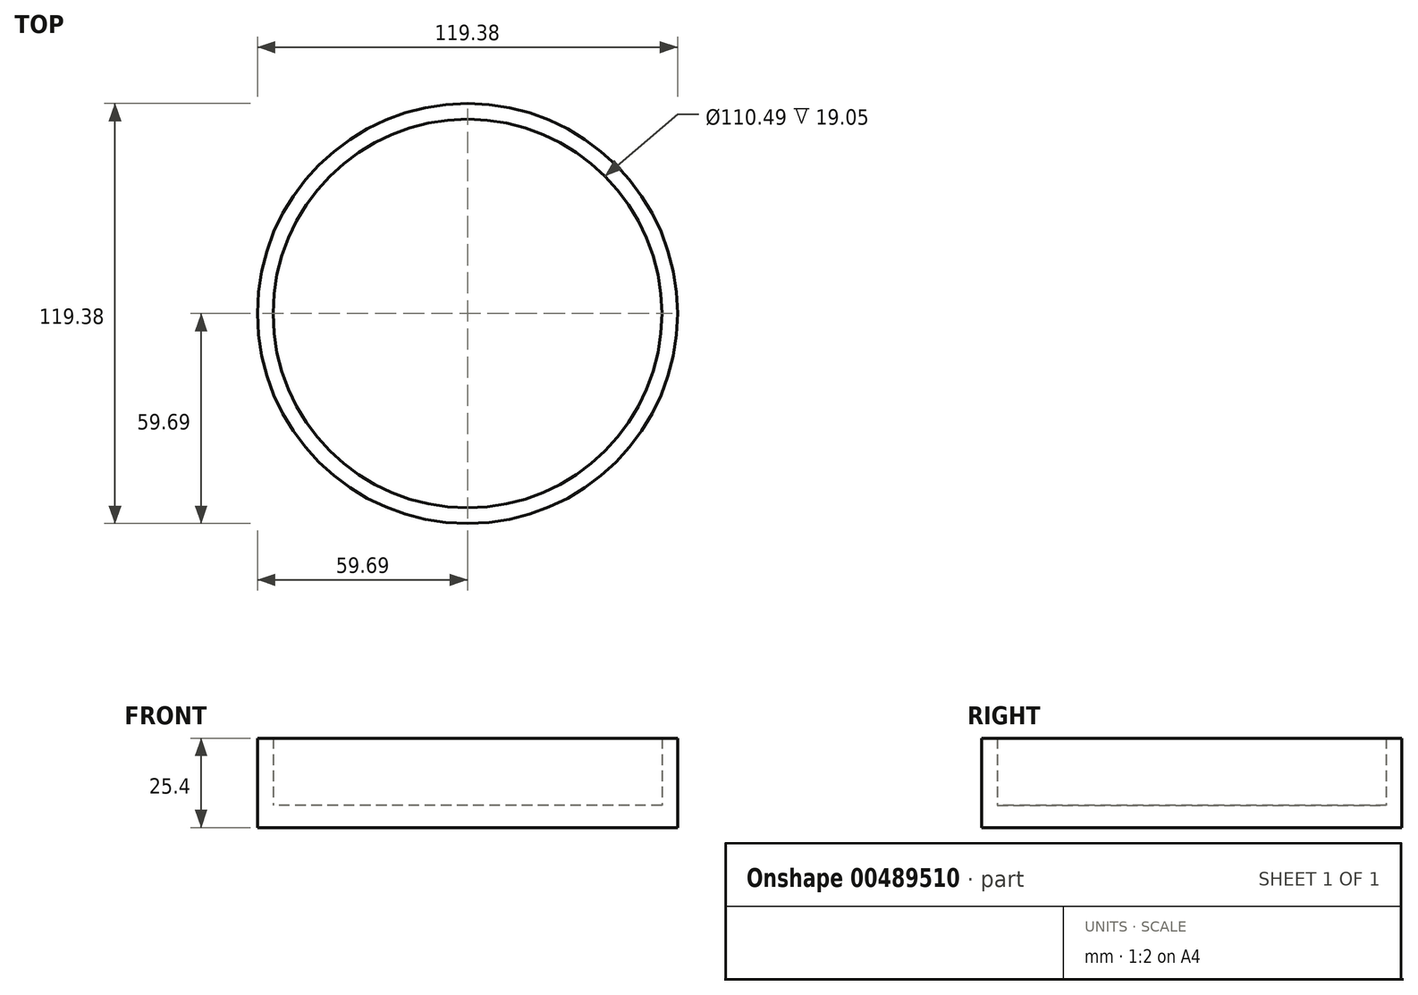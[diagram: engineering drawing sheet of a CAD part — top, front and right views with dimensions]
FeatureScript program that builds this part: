
annotation { "Feature Type Name" : "Feature", "Feature Type Description" : "" }
export const myFeature = defineFeature(function(context is Context, id is Id, definition is map)
    precondition{}
    {
        {
            var Q0;
            Q0=qCreatedBy(makeId("Top.planeOp"),FACE);
            var sketch = newSketch(context, id + "F0", { "sketchPlane" : qUnion([Q0])});
            skCircle(sketch, "E0", {"center": v(0, 0) * mm, "radius": 55.25 * mm});
            skCircle(sketch, "E1", {"center": v(0, 0) * mm, "radius": 59.7 * mm});
            skSolve(sketch);
        }
        {
            var Q0;
            Q0=makeQuery(id+"F0.imprint","IMPRINT",FACE,{"disambiguationData":[TD([[makeQuery(id+"F0.imprint","IMPRINT",EDGE,{"derivedFrom":sQuery(id+"F0.wireOp",EDGE,"E0")}),1.0]])]});
            var Q1;
            Q1=makeQuery(id+"F0.imprint","IMPRINT",FACE,{"disambiguationData":[TD([[makeQuery(id+"F0.imprint","IMPRINT",EDGE,{"derivedFrom":sQuery(id+"F0.wireOp",EDGE,"E0")}),-1.0]])]});
            extrude(context, id + "F1", {"entities" : qUnion([Q0, Q1]), "oppositeDirection" : true, "depth" : 6.35 * mm, "offsetDistance" : 25.4 * mm});
        }
        {
            var Q0;
            Q0=makeQuery(id+"F0.imprint","IMPRINT",FACE,{"disambiguationData":[TD([[makeQuery(id+"F0.imprint","IMPRINT",EDGE,{"derivedFrom":sQuery(id+"F0.wireOp",EDGE,"E0")}),-1.0]])]});
            extrude(context, id + "F2", {"entities" : qUnion([Q0]), "operationType" : NewBodyOperationType.ADD, "depth" : 19.05 * mm, "offsetDistance" : 25.4 * mm});
        }
    });
